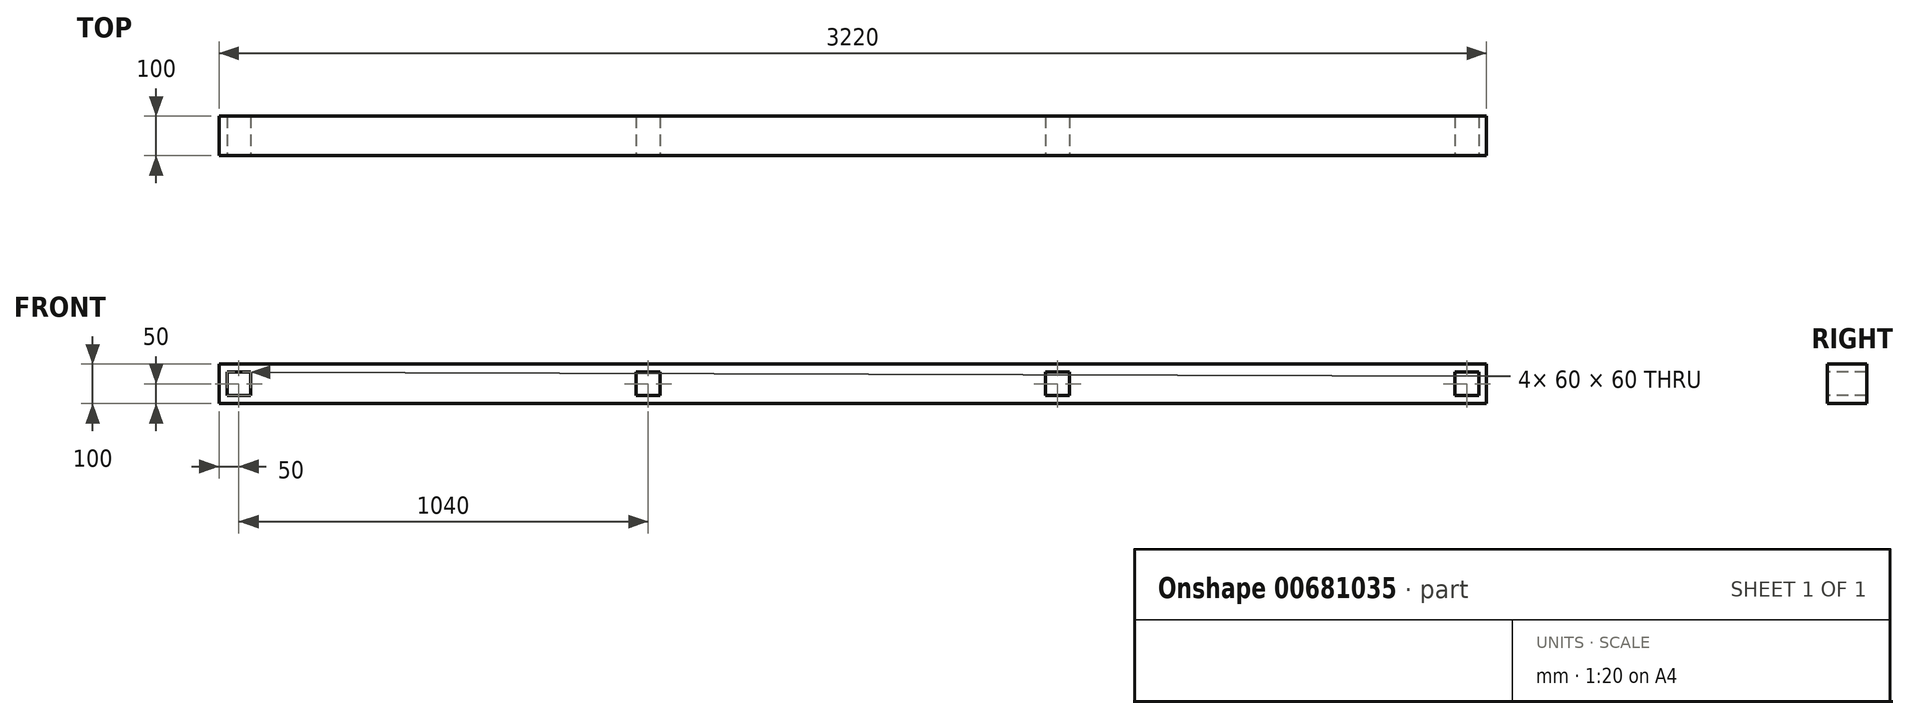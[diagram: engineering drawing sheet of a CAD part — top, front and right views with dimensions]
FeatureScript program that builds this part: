
annotation { "Feature Type Name" : "Feature", "Feature Type Description" : "" }
export const myFeature = defineFeature(function(context is Context, id is Id, definition is map)
    precondition{}
    {
        {
            var Q0;
            Q0=qCreatedBy(makeId("Front.planeOp"),FACE);
            var sketch = newSketch(context, id + "F0", { "sketchPlane" : qUnion([Q0])});
            skLineSegment(sketch, "E0.bottom", {"start": v(0, 0) * mm, "end": v(3220, 0) * mm});
            skLineSegment(sketch, "E0.top", {"start": v(0, 100) * mm, "end": v(3220, 100) * mm});
            skLineSegment(sketch, "E0.left", {"start": v(0, 0) * mm, "end": v(0, 100) * mm});
            skLineSegment(sketch, "E0.right", {"start": v(3220, 0) * mm, "end": v(3220, 100) * mm});
            skSolve(sketch);
        }
        {
            var Q0;
            Q0 = qSketchRegion(id + "F0", true);
            extrude(context, id + "F1", {"entities" : qUnion([Q0]), "depth" : 100 * mm, "offsetDistance" : 25 * mm});
        }
        {
            var Q0;
            Q0=makeQuery(id+"F1.opExtrude","CAP_FACE",FACE,{"disambiguationData":[OSD([sQuery(id+"F0.wireOp",EDGE,"E0.bottom"),sQuery(id+"F0.wireOp",EDGE,"E0.top"),sQuery(id+"F0.wireOp",EDGE,"E0.left"),sQuery(id+"F0.wireOp",EDGE,"E0.right")])],"isStart":false});
            var sketch = newSketch(context, id + "F2", { "sketchPlane" : qUnion([Q0])});
            skLineSegment(sketch, "E1.bottom", {"start": v(20, 20) * mm, "end": v(80, 20) * mm});
            skLineSegment(sketch, "E1.top", {"start": v(20, 80) * mm, "end": v(80, 80) * mm});
            skLineSegment(sketch, "E1.left", {"start": v(20, 20) * mm, "end": v(20, 80) * mm});
            skLineSegment(sketch, "E1.right", {"start": v(80, 20) * mm, "end": v(80, 80) * mm});
            skLineSegment(sketch, "E2.bottom", {"start": v(1060, 80) * mm, "end": v(1120, 80) * mm});
            skLineSegment(sketch, "E2.top", {"start": v(1060, 20) * mm, "end": v(1120, 20) * mm});
            skLineSegment(sketch, "E2.left", {"start": v(1060, 80) * mm, "end": v(1060, 20) * mm});
            skLineSegment(sketch, "E2.right", {"start": v(1120, 80) * mm, "end": v(1120, 20) * mm});
            skLineSegment(sketch, "E3.bottom", {"start": v(2100, 80) * mm, "end": v(2160, 80) * mm});
            skLineSegment(sketch, "E3.top", {"start": v(2100, 20) * mm, "end": v(2160, 20) * mm});
            skLineSegment(sketch, "E3.left", {"start": v(2100, 80) * mm, "end": v(2100, 20) * mm});
            skLineSegment(sketch, "E3.right", {"start": v(2160, 80) * mm, "end": v(2160, 20) * mm});
            skLineSegment(sketch, "E4.bottom", {"start": v(3140, 80) * mm, "end": v(3200, 80) * mm});
            skLineSegment(sketch, "E4.top", {"start": v(3140, 20) * mm, "end": v(3200, 20) * mm});
            skLineSegment(sketch, "E4.left", {"start": v(3140, 80) * mm, "end": v(3140, 20) * mm});
            skLineSegment(sketch, "E4.right", {"start": v(3200, 80) * mm, "end": v(3200, 20) * mm});
            skSolve(sketch);
        }
        {
            var Q0;
            Q0 = qSketchRegion(id + "F2", true);
            extrude(context, id + "F3", {"entities" : qUnion([Q0]), "operationType" : NewBodyOperationType.REMOVE, "endBound" : BoundingType.THROUGH_ALL, "oppositeDirection" : true, "depth" : 25 * mm, "offsetDistance" : 25 * mm});
        }
    });
